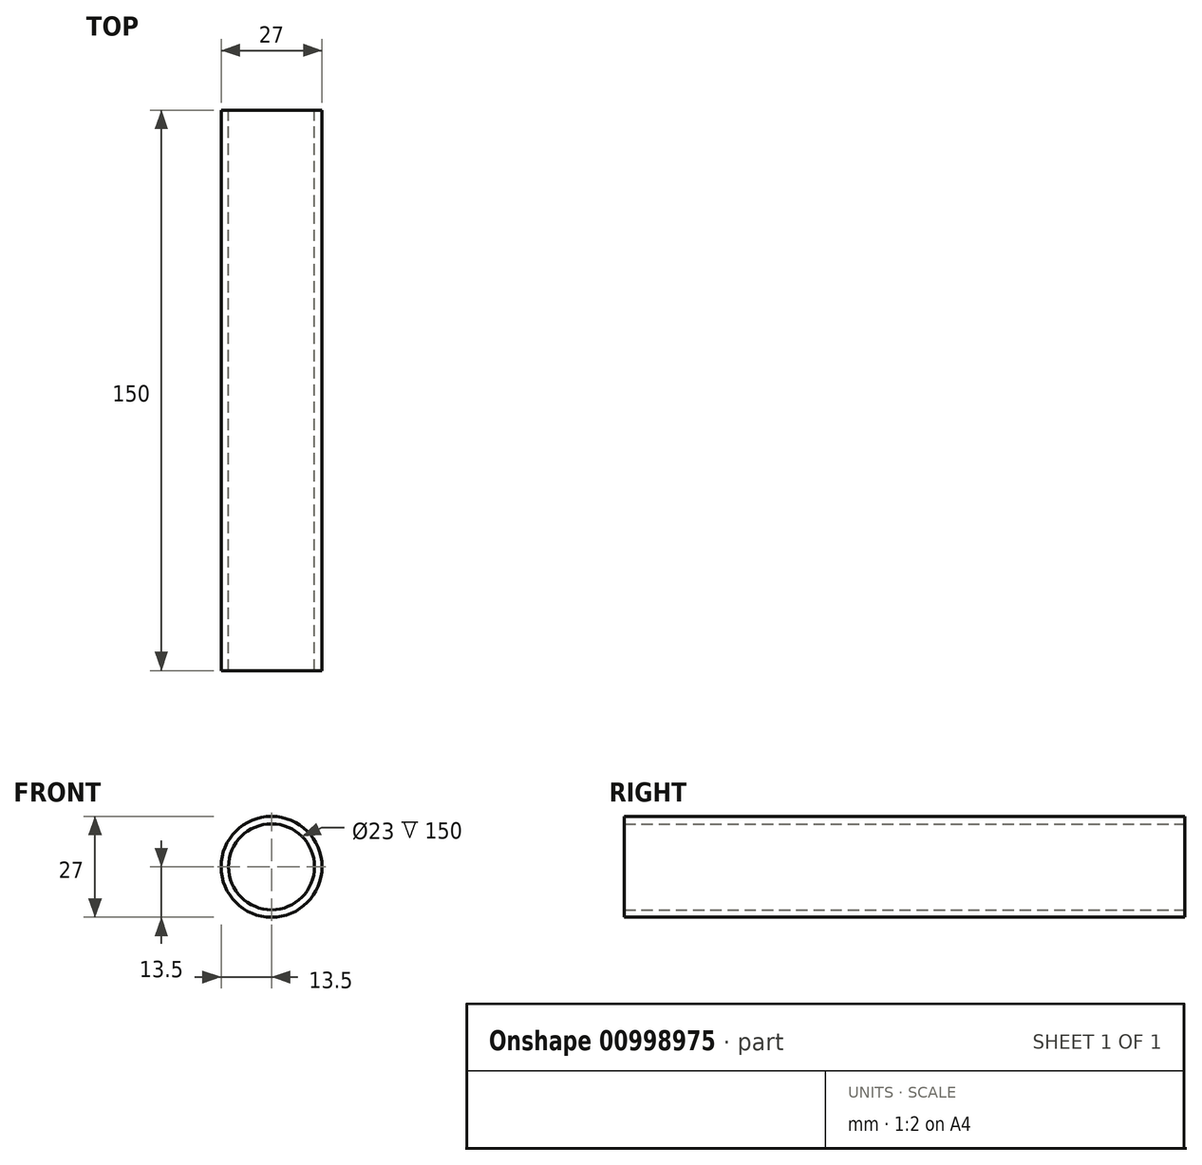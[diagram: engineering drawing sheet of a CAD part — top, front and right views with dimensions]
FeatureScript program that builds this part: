
annotation { "Feature Type Name" : "Feature", "Feature Type Description" : "" }
export const myFeature = defineFeature(function(context is Context, id is Id, definition is map)
    precondition{}
    {
        {
            var Q0;
            Q0=qCreatedBy(makeId("Front.planeOp"),FACE);
            var sketch = newSketch(context, id + "F0", { "sketchPlane" : qUnion([Q0])});
            skCircle(sketch, "E0", {"center": v(0, 0) * mm, "radius": 11.5 * mm});
            skCircle(sketch, "E1", {"center": v(0, 0) * mm, "radius": 13.5 * mm});
            skSolve(sketch);
        }
        {
            var Q0;
            Q0 = qSketchRegion(id + "F0", true);
            extrude(context, id + "F1", {"entities" : qUnion([Q0]), "depth" : 150 * mm, "offsetDistance" : 25 * mm});
        }
    });
